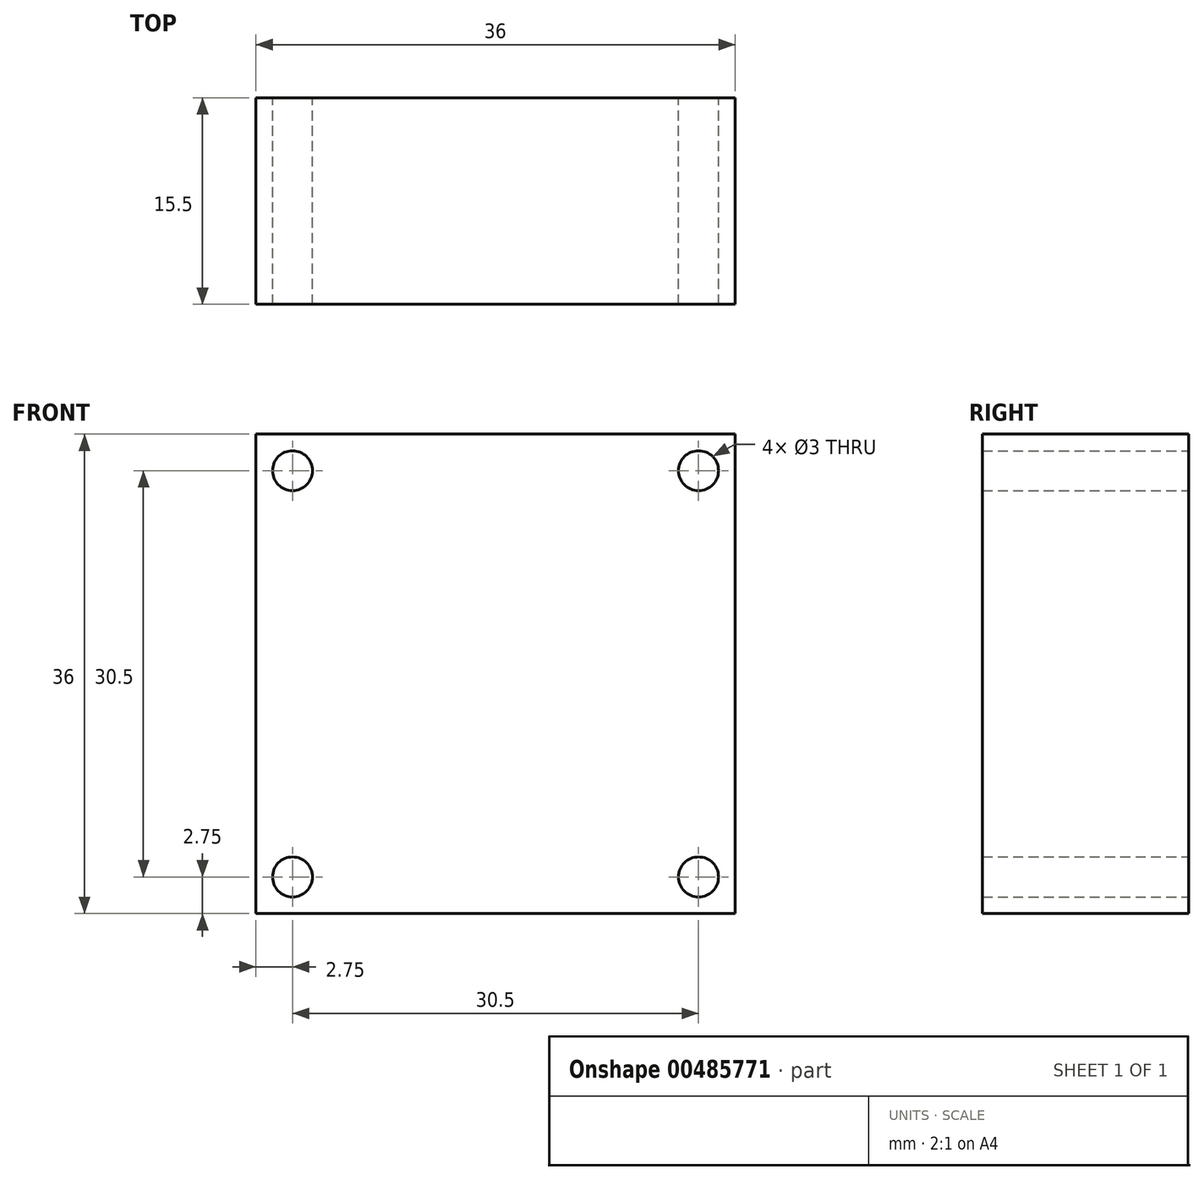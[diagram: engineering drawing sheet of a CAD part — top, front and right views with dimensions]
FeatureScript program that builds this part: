
annotation { "Feature Type Name" : "Feature", "Feature Type Description" : "" }
export const myFeature = defineFeature(function(context is Context, id is Id, definition is map)
    precondition{}
    {
        {
            var Q0;
            Q0=qCreatedBy(makeId("Front.planeOp"),FACE);
            var sketch = newSketch(context, id + "F0", { "sketchPlane" : qUnion([Q0])});
            skLineSegment(sketch, "E0.bottom", {"start": v(18, 18) * mm, "end": v(-18, 18) * mm});
            skLineSegment(sketch, "E0.top", {"start": v(18, -18) * mm, "end": v(-18, -18) * mm});
            skLineSegment(sketch, "E0.left", {"start": v(18, 18) * mm, "end": v(18, -18) * mm});
            skLineSegment(sketch, "E0.right", {"start": v(-18, 18) * mm, "end": v(-18, -18) * mm});
            skPoint(sketch, "E0.middle", {"position": v(0, 0) * mm});
            skCircle(sketch, "E1", {"center": v(-15.25, 15.25) * mm, "radius": 1.5 * mm});
            skCircle(sketch, "E2", {"center": v(15.25, 15.25) * mm, "radius": 1.5 * mm});
            skCircle(sketch, "E3", {"center": v(15.25, -15.25) * mm, "radius": 1.5 * mm});
            skCircle(sketch, "E4", {"center": v(-15.25, -15.25) * mm, "radius": 1.5 * mm});
            skSolve(sketch);
        }
        {
            var Q0;
            Q0 = qSketchRegion(id + "F0", true);
            extrude(context, id + "F1", {"entities" : qUnion([Q0]), "depth" : 15.5 * mm, "offsetDistance" : 25 * mm});
        }
    });
